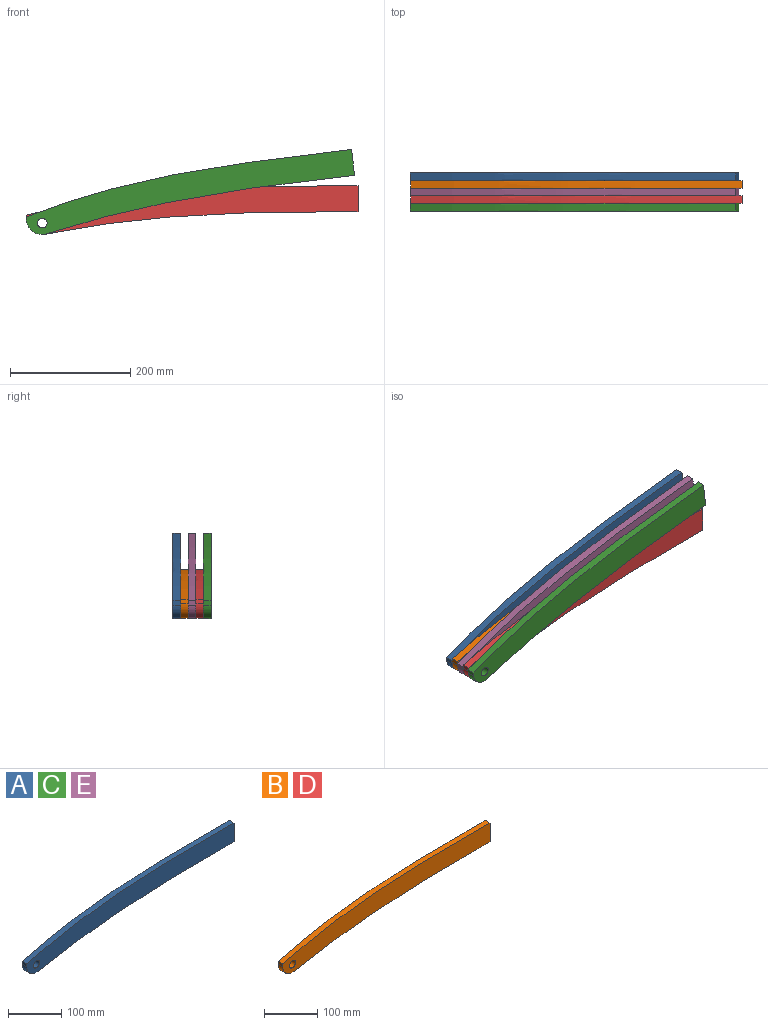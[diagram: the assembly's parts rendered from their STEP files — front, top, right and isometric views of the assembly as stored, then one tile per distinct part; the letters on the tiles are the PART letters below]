
ASSEMBLY  parts=5 mates=1
PART A: 8 faces, bbox 550.7x12.7x81.4 mm
  f0: plane 43.38x12.7mm, normal (1,0,0), area 551mm2, adj f1,f4,f6,f7
  f1: extruded ~550.72x48.97mm, area 7043.6mm2, adj f0,f2,f6,f7
  f2: plane 12.7x7mm, normal (-1,0,0), area 88.9mm2, adj f1,f3,f6,f7
  f3: cylinder r=25.4mm len=30.39mm, axis (0,1,0), area 570.5mm2, adj f2,f4,f6,f7
  f4: extruded ~520.33x37.78mm, area 6637.7mm2, adj f0,f3,f6,f7
  f5: cylinder r=8.01mm len=16.02mm, axis (0,1,0), area 639.3mm2, adj f6,f7
  f6: plane 550.72x81.38mm, normal (0,-1,0), area 22992.2mm2, adj f0,f1,f2,f3,f4,f5
  f7: plane 550.72x81.38mm, normal (0,1,0), area 22992.2mm2, adj f0,f1,f2,f3,f4,f5
PART B: 8 faces, bbox 550.7x12.7x81.4 mm
  f0: plane 43.38x12.7mm, normal (1,0,0), area 551mm2, adj f1,f4,f6,f7
  f1: extruded ~550.72x48.97mm, area 7043.6mm2, adj f0,f2,f6,f7
  f2: plane 12.7x7mm, normal (-1,0,0), area 88.9mm2, adj f1,f3,f6,f7
  f3: cylinder r=25.4mm len=30.39mm, axis (0,1,0), area 570.5mm2, adj f2,f4,f6,f7
  f4: extruded ~520.33x37.78mm, area 6637.7mm2, adj f0,f3,f6,f7
  f5: cylinder r=8.01mm len=16.02mm, axis (0,1,0), area 639.3mm2, adj f6,f7
  f6: plane 550.72x81.38mm, normal (0,-1,0), area 22992.2mm2, adj f0,f1,f2,f3,f4,f5
  f7: plane 550.72x81.38mm, normal (0,1,0), area 22992.2mm2, adj f0,f1,f2,f3,f4,f5
PART C: same geometry as A
PART D: same geometry as B
PART E: same geometry as A
PLACE A rot(axis=(0,-1,0),6.6deg) t=(-670.1,1323.82,-1209.37)mm
PLACE B t=(-846.99,1285.72,-954.37)mm fixed
PLACE C rot(axis=(0,-1,0),6.6deg) t=(-670.1,1273.02,-1209.37)mm
PLACE D t=(-846.99,1260.32,-954.37)mm fixed
PLACE E rot(axis=(0,-1,0),6.6deg) t=(-670.1,1298.42,-1209.37)mm
MATE revolute A.f5 <-> B.f5  axis (0,1,0) through (1446.23,1311.12,447.55)mm
